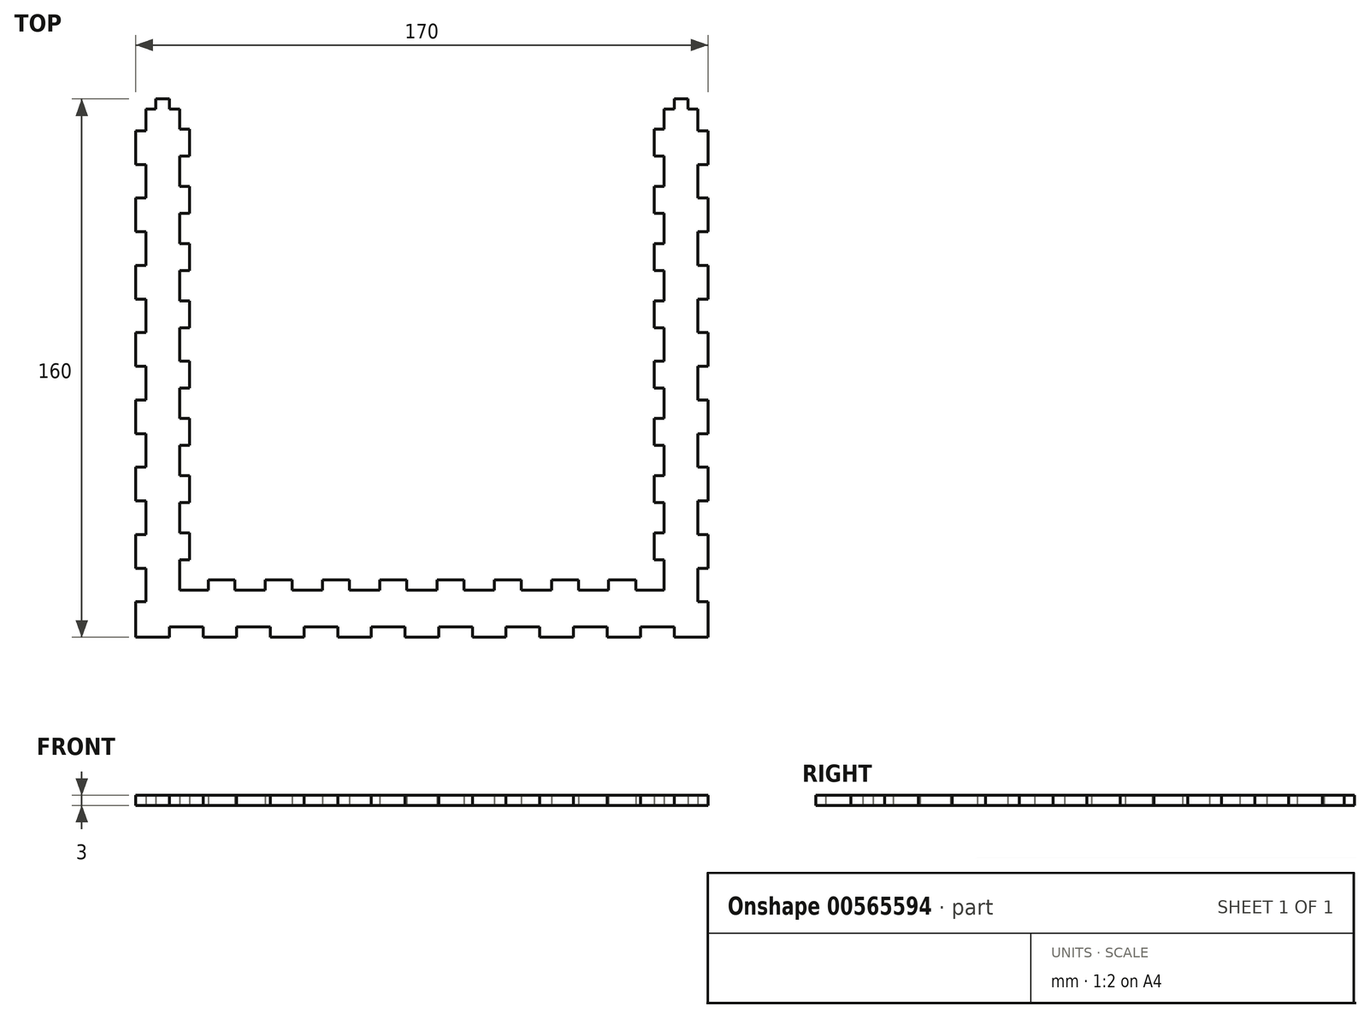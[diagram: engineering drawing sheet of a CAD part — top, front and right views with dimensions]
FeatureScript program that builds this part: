
annotation { "Feature Type Name" : "Feature", "Feature Type Description" : "" }
export const myFeature = defineFeature(function(context is Context, id is Id, definition is map)
    precondition{}
    {
        {
            var Q0;
            Q0=qCreatedBy(makeId("Top.planeOp"),FACE);
            var sketch = newSketch(context, id + "F0", { "sketchPlane" : qUnion([Q0])});
            skLineSegment(sketch, "E0.bottom", {"start": v(0, 0) * mm, "end": v(10, 0) * mm});
            skLineSegment(sketch, "E0.top", {"start": v(6, 160) * mm, "end": v(10, 160) * mm});
            skLineSegment(sketch, "E0.left", {"start": v(0, 0) * mm, "end": v(0, 10.5) * mm});
            skLineSegment(sketch, "E0.right", {"start": v(170, 0) * mm, "end": v(170, 10.5) * mm});
            skLineSegment(sketch, "E1.top", {"start": v(21.5, 17) * mm, "end": v(29.5, 17) * mm});
            skLineSegment(sketch, "E1.left", {"start": v(16, 151) * mm, "end": v(16, 143) * mm});
            skLineSegment(sketch, "E1.right", {"start": v(154, 151) * mm, "end": v(154, 143) * mm});
            skLineSegment(sketch, "E2.top", {"start": v(16, 151) * mm, "end": v(13, 151) * mm});
            skLineSegment(sketch, "E2.right", {"start": v(13, 157) * mm, "end": v(13, 151) * mm});
            skLineSegment(sketch, "E3.bottom", {"start": v(16, 143) * mm, "end": v(13, 143) * mm});
            skLineSegment(sketch, "E3.top", {"start": v(16, 134) * mm, "end": v(13, 134) * mm});
            skLineSegment(sketch, "E3.right", {"start": v(13, 143) * mm, "end": v(13, 134) * mm});
            skLineSegment(sketch, "E4.bottom", {"start": v(16, 126) * mm, "end": v(13, 126) * mm});
            skLineSegment(sketch, "E4.top", {"start": v(16, 117) * mm, "end": v(13, 117) * mm});
            skLineSegment(sketch, "E4.right", {"start": v(13, 126) * mm, "end": v(13, 117) * mm});
            skLineSegment(sketch, "E5.bottom", {"start": v(16, 109) * mm, "end": v(13, 109) * mm});
            skLineSegment(sketch, "E5.top", {"start": v(16, 100) * mm, "end": v(13, 100) * mm});
            skLineSegment(sketch, "E5.right", {"start": v(13, 109) * mm, "end": v(13, 100) * mm});
            skLineSegment(sketch, "E6.bottom", {"start": v(16, 92) * mm, "end": v(13, 92) * mm});
            skLineSegment(sketch, "E6.top", {"start": v(16, 82) * mm, "end": v(13, 82) * mm});
            skLineSegment(sketch, "E6.right", {"start": v(13, 92) * mm, "end": v(13, 82) * mm});
            skLineSegment(sketch, "E7.bottom", {"start": v(16, 74) * mm, "end": v(13, 74) * mm});
            skLineSegment(sketch, "E7.top", {"start": v(16, 65) * mm, "end": v(13, 65) * mm});
            skLineSegment(sketch, "E7.right", {"start": v(13, 74) * mm, "end": v(13, 65) * mm});
            skLineSegment(sketch, "E8.bottom", {"start": v(13, 57) * mm, "end": v(16, 57) * mm});
            skLineSegment(sketch, "E8.top", {"start": v(13, 48) * mm, "end": v(16, 48) * mm});
            skLineSegment(sketch, "E8.left", {"start": v(13, 57) * mm, "end": v(13, 48) * mm});
            skLineSegment(sketch, "E9.bottom", {"start": v(16, 40) * mm, "end": v(13, 40) * mm});
            skLineSegment(sketch, "E9.top", {"start": v(16, 31) * mm, "end": v(13, 31) * mm});
            skLineSegment(sketch, "E9.right", {"start": v(13, 40) * mm, "end": v(13, 31) * mm});
            skLineSegment(sketch, "E10.bottom", {"start": v(13, 14) * mm, "end": v(21.5, 14) * mm});
            skLineSegment(sketch, "E10.top", {"start": v(13, 23) * mm, "end": v(16, 23) * mm});
            skLineSegment(sketch, "E10.left", {"start": v(13, 14) * mm, "end": v(13, 23) * mm});
            skLineSegment(sketch, "E10.right", {"start": v(21.5, 14) * mm, "end": v(21.5, 17) * mm});
            skLineSegment(sketch, "E11.bottom", {"start": v(29.5, 14) * mm, "end": v(38.5, 14) * mm});
            skLineSegment(sketch, "E11.left", {"start": v(29.5, 14) * mm, "end": v(29.5, 17) * mm});
            skLineSegment(sketch, "E11.right", {"start": v(38.5, 14) * mm, "end": v(38.5, 17) * mm});
            skLineSegment(sketch, "E12.bottom", {"start": v(46.5, 14) * mm, "end": v(55.5, 14) * mm});
            skLineSegment(sketch, "E12.left", {"start": v(46.5, 14) * mm, "end": v(46.5, 17) * mm});
            skLineSegment(sketch, "E12.right", {"start": v(55.5, 14) * mm, "end": v(55.5, 17) * mm});
            skLineSegment(sketch, "E13.bottom", {"start": v(63.5, 14) * mm, "end": v(72.5, 14) * mm});
            skLineSegment(sketch, "E13.left", {"start": v(63.5, 14) * mm, "end": v(63.5, 17) * mm});
            skLineSegment(sketch, "E13.right", {"start": v(72.5, 14) * mm, "end": v(72.5, 17) * mm});
            skLineSegment(sketch, "E14.bottom", {"start": v(80.5, 14) * mm, "end": v(89.5, 14) * mm});
            skLineSegment(sketch, "E14.left", {"start": v(80.5, 14) * mm, "end": v(80.5, 17) * mm});
            skLineSegment(sketch, "E14.right", {"start": v(89.5, 14) * mm, "end": v(89.5, 17) * mm});
            skLineSegment(sketch, "E15.bottom", {"start": v(97.5, 14) * mm, "end": v(106.5, 14) * mm});
            skLineSegment(sketch, "E15.left", {"start": v(97.5, 14) * mm, "end": v(97.5, 17) * mm});
            skLineSegment(sketch, "E15.right", {"start": v(106.5, 14) * mm, "end": v(106.5, 17) * mm});
            skLineSegment(sketch, "E16.bottom", {"start": v(114.5, 14) * mm, "end": v(123.5, 14) * mm});
            skLineSegment(sketch, "E16.left", {"start": v(114.5, 14) * mm, "end": v(114.5, 17) * mm});
            skLineSegment(sketch, "E16.right", {"start": v(123.5, 14) * mm, "end": v(123.5, 17) * mm});
            skLineSegment(sketch, "E17.bottom", {"start": v(131.5, 14) * mm, "end": v(140.5, 14) * mm});
            skLineSegment(sketch, "E17.left", {"start": v(131.5, 14) * mm, "end": v(131.5, 17) * mm});
            skLineSegment(sketch, "E17.right", {"start": v(140.5, 14) * mm, "end": v(140.5, 17) * mm});
            skLineSegment(sketch, "E18.bottom", {"start": v(148.5, 14) * mm, "end": v(157, 14) * mm});
            skLineSegment(sketch, "E18.top", {"start": v(154, 23) * mm, "end": v(157, 23) * mm});
            skLineSegment(sketch, "E18.left", {"start": v(148.5, 14) * mm, "end": v(148.5, 17) * mm});
            skLineSegment(sketch, "E18.right", {"start": v(157, 14) * mm, "end": v(157, 23) * mm});
            skLineSegment(sketch, "E19.bottom", {"start": v(157, 31) * mm, "end": v(154, 31) * mm});
            skLineSegment(sketch, "E19.top", {"start": v(157, 40) * mm, "end": v(154, 40) * mm});
            skLineSegment(sketch, "E19.left", {"start": v(157, 31) * mm, "end": v(157, 40) * mm});
            skLineSegment(sketch, "E20.bottom", {"start": v(157, 48) * mm, "end": v(154, 48) * mm});
            skLineSegment(sketch, "E20.top", {"start": v(157, 57) * mm, "end": v(154, 57) * mm});
            skLineSegment(sketch, "E20.left", {"start": v(157, 48) * mm, "end": v(157, 57) * mm});
            skLineSegment(sketch, "E21.bottom", {"start": v(157, 65) * mm, "end": v(154, 65) * mm});
            skLineSegment(sketch, "E21.top", {"start": v(157, 74) * mm, "end": v(154, 74) * mm});
            skLineSegment(sketch, "E21.left", {"start": v(157, 65) * mm, "end": v(157, 74) * mm});
            skLineSegment(sketch, "E22.bottom", {"start": v(157, 82) * mm, "end": v(154, 82) * mm});
            skLineSegment(sketch, "E22.top", {"start": v(157, 92) * mm, "end": v(154, 92) * mm});
            skLineSegment(sketch, "E22.left", {"start": v(157, 82) * mm, "end": v(157, 92) * mm});
            skLineSegment(sketch, "E23.bottom", {"start": v(157, 100) * mm, "end": v(154, 100) * mm});
            skLineSegment(sketch, "E23.top", {"start": v(157, 109) * mm, "end": v(154, 109) * mm});
            skLineSegment(sketch, "E23.left", {"start": v(157, 100) * mm, "end": v(157, 109) * mm});
            skLineSegment(sketch, "E24.bottom", {"start": v(157, 117) * mm, "end": v(154, 117) * mm});
            skLineSegment(sketch, "E24.top", {"start": v(157, 126) * mm, "end": v(154, 126) * mm});
            skLineSegment(sketch, "E24.left", {"start": v(157, 117) * mm, "end": v(157, 126) * mm});
            skLineSegment(sketch, "E25.bottom", {"start": v(157, 134) * mm, "end": v(154, 134) * mm});
            skLineSegment(sketch, "E25.top", {"start": v(157, 143) * mm, "end": v(154, 143) * mm});
            skLineSegment(sketch, "E25.left", {"start": v(157, 134) * mm, "end": v(157, 143) * mm});
            skLineSegment(sketch, "E26.bottom", {"start": v(157, 151) * mm, "end": v(154, 151) * mm});
            skLineSegment(sketch, "E26.left", {"start": v(157, 151) * mm, "end": v(157, 157) * mm});
            skLineSegment(sketch, "E27.top", {"start": v(13, 157) * mm, "end": v(10, 157) * mm});
            skLineSegment(sketch, "E27.right", {"start": v(10, 160) * mm, "end": v(10, 157) * mm});
            skLineSegment(sketch, "E28.top", {"start": v(3, 157) * mm, "end": v(6, 157) * mm});
            skLineSegment(sketch, "E28.right", {"start": v(6, 160) * mm, "end": v(6, 157) * mm});
            skLineSegment(sketch, "E29.top", {"start": v(0, 150.5) * mm, "end": v(3, 150.5) * mm});
            skLineSegment(sketch, "E29.right", {"start": v(3, 157) * mm, "end": v(3, 150.5) * mm});
            skLineSegment(sketch, "E30.bottom", {"start": v(3, 140.5) * mm, "end": v(0, 140.5) * mm});
            skLineSegment(sketch, "E30.top", {"start": v(3, 130.5) * mm, "end": v(0, 130.5) * mm});
            skLineSegment(sketch, "E30.left", {"start": v(3, 140.5) * mm, "end": v(3, 130.5) * mm});
            skLineSegment(sketch, "E31.bottom", {"start": v(3, 120.5) * mm, "end": v(0, 120.5) * mm});
            skLineSegment(sketch, "E31.top", {"start": v(3, 110.5) * mm, "end": v(0, 110.5) * mm});
            skLineSegment(sketch, "E31.left", {"start": v(3, 120.5) * mm, "end": v(3, 110.5) * mm});
            skLineSegment(sketch, "E32.bottom", {"start": v(3, 100.5) * mm, "end": v(0, 100.5) * mm});
            skLineSegment(sketch, "E32.top", {"start": v(3, 90.5) * mm, "end": v(0, 90.5) * mm});
            skLineSegment(sketch, "E32.left", {"start": v(3, 100.5) * mm, "end": v(3, 90.5) * mm});
            skLineSegment(sketch, "E33.bottom", {"start": v(3, 80.5) * mm, "end": v(0, 80.5) * mm});
            skLineSegment(sketch, "E33.top", {"start": v(3, 70.5) * mm, "end": v(0, 70.5) * mm});
            skLineSegment(sketch, "E33.left", {"start": v(3, 80.5) * mm, "end": v(3, 70.5) * mm});
            skLineSegment(sketch, "E34.bottom", {"start": v(3, 60.5) * mm, "end": v(0, 60.5) * mm});
            skLineSegment(sketch, "E34.top", {"start": v(3, 50.5) * mm, "end": v(0, 50.5) * mm});
            skLineSegment(sketch, "E34.left", {"start": v(3, 60.5) * mm, "end": v(3, 50.5) * mm});
            skLineSegment(sketch, "E35.bottom", {"start": v(3, 40.5) * mm, "end": v(0, 40.5) * mm});
            skLineSegment(sketch, "E35.top", {"start": v(3, 30.5) * mm, "end": v(0, 30.5) * mm});
            skLineSegment(sketch, "E35.left", {"start": v(3, 40.5) * mm, "end": v(3, 30.5) * mm});
            skLineSegment(sketch, "E36.bottom", {"start": v(3, 20.5) * mm, "end": v(0, 20.5) * mm});
            skLineSegment(sketch, "E36.top", {"start": v(3, 10.5) * mm, "end": v(0, 10.5) * mm});
            skLineSegment(sketch, "E36.left", {"start": v(3, 20.5) * mm, "end": v(3, 10.5) * mm});
            skLineSegment(sketch, "E37.top", {"start": v(10, 3) * mm, "end": v(20, 3) * mm});
            skLineSegment(sketch, "E37.left", {"start": v(10, 0) * mm, "end": v(10, 3) * mm});
            skLineSegment(sketch, "E37.right", {"start": v(20, 0) * mm, "end": v(20, 3) * mm});
            skLineSegment(sketch, "E38.bottom", {"start": v(30, 3) * mm, "end": v(40, 3) * mm});
            skLineSegment(sketch, "E38.left", {"start": v(30, 3) * mm, "end": v(30, 0) * mm});
            skLineSegment(sketch, "E38.right", {"start": v(40, 3) * mm, "end": v(40, 0) * mm});
            skLineSegment(sketch, "E39.bottom", {"start": v(50, 3) * mm, "end": v(60, 3) * mm});
            skLineSegment(sketch, "E39.left", {"start": v(50, 3) * mm, "end": v(50, 0) * mm});
            skLineSegment(sketch, "E39.right", {"start": v(60, 3) * mm, "end": v(60, 0) * mm});
            skLineSegment(sketch, "E40.bottom", {"start": v(70, 3) * mm, "end": v(80, 3) * mm});
            skLineSegment(sketch, "E40.left", {"start": v(70, 3) * mm, "end": v(70, 0) * mm});
            skLineSegment(sketch, "E40.right", {"start": v(80, 3) * mm, "end": v(80, 0) * mm});
            skLineSegment(sketch, "E41.bottom", {"start": v(90, 3) * mm, "end": v(100, 3) * mm});
            skLineSegment(sketch, "E41.left", {"start": v(90, 3) * mm, "end": v(90, 0) * mm});
            skLineSegment(sketch, "E41.right", {"start": v(100, 3) * mm, "end": v(100, 0) * mm});
            skLineSegment(sketch, "E42.bottom", {"start": v(110, 3) * mm, "end": v(120, 3) * mm});
            skLineSegment(sketch, "E42.left", {"start": v(110, 3) * mm, "end": v(110, 0) * mm});
            skLineSegment(sketch, "E42.right", {"start": v(120, 3) * mm, "end": v(120, 0) * mm});
            skLineSegment(sketch, "E43.bottom", {"start": v(130, 3) * mm, "end": v(140, 3) * mm});
            skLineSegment(sketch, "E43.left", {"start": v(130, 3) * mm, "end": v(130, 0) * mm});
            skLineSegment(sketch, "E43.right", {"start": v(140, 3) * mm, "end": v(140, 0) * mm});
            skLineSegment(sketch, "E44.bottom", {"start": v(150, 3) * mm, "end": v(160, 3) * mm});
            skLineSegment(sketch, "E44.left", {"start": v(150, 3) * mm, "end": v(150, 0) * mm});
            skLineSegment(sketch, "E44.right", {"start": v(160, 3) * mm, "end": v(160, 0) * mm});
            skLineSegment(sketch, "E45.bottom", {"start": v(170, 10.5) * mm, "end": v(167, 10.5) * mm});
            skLineSegment(sketch, "E45.top", {"start": v(170, 20.5) * mm, "end": v(167, 20.5) * mm});
            skLineSegment(sketch, "E45.right", {"start": v(167, 10.5) * mm, "end": v(167, 20.5) * mm});
            skLineSegment(sketch, "E46.bottom", {"start": v(170, 30.5) * mm, "end": v(167, 30.5) * mm});
            skLineSegment(sketch, "E46.top", {"start": v(170, 40.5) * mm, "end": v(167, 40.5) * mm});
            skLineSegment(sketch, "E46.right", {"start": v(167, 30.5) * mm, "end": v(167, 40.5) * mm});
            skLineSegment(sketch, "E47.bottom", {"start": v(167, 50.5) * mm, "end": v(170, 50.5) * mm});
            skLineSegment(sketch, "E47.top", {"start": v(167, 60.5) * mm, "end": v(170, 60.5) * mm});
            skLineSegment(sketch, "E47.left", {"start": v(167, 50.5) * mm, "end": v(167, 60.5) * mm});
            skLineSegment(sketch, "E48.bottom", {"start": v(167, 70.5) * mm, "end": v(170, 70.5) * mm});
            skLineSegment(sketch, "E48.top", {"start": v(167, 80.5) * mm, "end": v(170, 80.5) * mm});
            skLineSegment(sketch, "E48.left", {"start": v(167, 70.5) * mm, "end": v(167, 80.5) * mm});
            skLineSegment(sketch, "E49.bottom", {"start": v(167, 90.5) * mm, "end": v(170, 90.5) * mm});
            skLineSegment(sketch, "E49.top", {"start": v(167, 100.5) * mm, "end": v(170, 100.5) * mm});
            skLineSegment(sketch, "E49.left", {"start": v(167, 90.5) * mm, "end": v(167, 100.5) * mm});
            skLineSegment(sketch, "E50.bottom", {"start": v(167, 110.5) * mm, "end": v(170, 110.5) * mm});
            skLineSegment(sketch, "E50.top", {"start": v(167, 120.5) * mm, "end": v(170, 120.5) * mm});
            skLineSegment(sketch, "E50.left", {"start": v(167, 110.5) * mm, "end": v(167, 120.5) * mm});
            skLineSegment(sketch, "E51.bottom", {"start": v(167, 130.5) * mm, "end": v(170, 130.5) * mm});
            skLineSegment(sketch, "E51.top", {"start": v(167, 140.5) * mm, "end": v(170, 140.5) * mm});
            skLineSegment(sketch, "E51.left", {"start": v(167, 130.5) * mm, "end": v(167, 140.5) * mm});
            skLineSegment(sketch, "E52.top", {"start": v(170, 150.5) * mm, "end": v(167, 150.5) * mm});
            skLineSegment(sketch, "E52.right", {"start": v(167, 157) * mm, "end": v(167, 150.5) * mm});
            skLineSegment(sketch, "E53.top", {"start": v(167, 157) * mm, "end": v(164, 157) * mm});
            skLineSegment(sketch, "E53.right", {"start": v(164, 160) * mm, "end": v(164, 157) * mm});
            skLineSegment(sketch, "E54.top", {"start": v(157, 157) * mm, "end": v(160, 157) * mm});
            skLineSegment(sketch, "E54.right", {"start": v(160, 160) * mm, "end": v(160, 157) * mm});
            skLineSegment(sketch, "E55.trimOffspring", {"start": v(160, 160) * mm, "end": v(164, 160) * mm});
            skLineSegment(sketch, "E56.trimOffspring", {"start": v(38.5, 17) * mm, "end": v(46.5, 17) * mm});
            skLineSegment(sketch, "E57.trimOffspring", {"start": v(16, 31) * mm, "end": v(16, 23) * mm});
            skLineSegment(sketch, "E58.trimOffspring", {"start": v(123.5, 17) * mm, "end": v(131.5, 17) * mm});
            skLineSegment(sketch, "E59.trimOffspring", {"start": v(140.5, 17) * mm, "end": v(148.5, 17) * mm});
            skLineSegment(sketch, "E60.trimOffspring", {"start": v(106.5, 17) * mm, "end": v(114.5, 17) * mm});
            skLineSegment(sketch, "E61.trimOffspring", {"start": v(89.5, 17) * mm, "end": v(97.5, 17) * mm});
            skLineSegment(sketch, "E62.trimOffspring", {"start": v(72.5, 17) * mm, "end": v(80.5, 17) * mm});
            skLineSegment(sketch, "E63.trimOffspring", {"start": v(55.5, 17) * mm, "end": v(63.5, 17) * mm});
            skLineSegment(sketch, "E64.trimOffspring", {"start": v(16, 48) * mm, "end": v(16, 40) * mm});
            skLineSegment(sketch, "E65.trimOffspring", {"start": v(0, 40.5) * mm, "end": v(0, 50.5) * mm});
            skLineSegment(sketch, "E66.trimOffspring", {"start": v(0, 60.5) * mm, "end": v(0, 70.5) * mm});
            skLineSegment(sketch, "E67.trimOffspring", {"start": v(0, 140.5) * mm, "end": v(0, 150.5) * mm});
            skLineSegment(sketch, "E68.trimOffspring", {"start": v(16, 134) * mm, "end": v(16, 126) * mm});
            skLineSegment(sketch, "E69.trimOffspring", {"start": v(16, 117) * mm, "end": v(16, 109) * mm});
            skLineSegment(sketch, "E70.trimOffspring", {"start": v(0, 120.5) * mm, "end": v(0, 130.5) * mm});
            skLineSegment(sketch, "E71.trimOffspring", {"start": v(16, 100) * mm, "end": v(16, 92) * mm});
            skLineSegment(sketch, "E72.trimOffspring", {"start": v(0, 100.5) * mm, "end": v(0, 110.5) * mm});
            skLineSegment(sketch, "E73.trimOffspring", {"start": v(16, 82) * mm, "end": v(16, 74) * mm});
            skLineSegment(sketch, "E74.trimOffspring", {"start": v(0, 80.5) * mm, "end": v(0, 90.5) * mm});
            skLineSegment(sketch, "E75.trimOffspring", {"start": v(16, 65) * mm, "end": v(16, 57) * mm});
            skLineSegment(sketch, "E76.trimOffspring", {"start": v(0, 20.5) * mm, "end": v(0, 30.5) * mm});
            skLineSegment(sketch, "E77.trimOffspring", {"start": v(20, 0) * mm, "end": v(30, 0) * mm});
            skLineSegment(sketch, "E78.trimOffspring", {"start": v(40, 0) * mm, "end": v(50, 0) * mm});
            skLineSegment(sketch, "E79.trimOffspring", {"start": v(60, 0) * mm, "end": v(70, 0) * mm});
            skLineSegment(sketch, "E80.trimOffspring", {"start": v(80, 0) * mm, "end": v(90, 0) * mm});
            skLineSegment(sketch, "E81.trimOffspring", {"start": v(100, 0) * mm, "end": v(110, 0) * mm});
            skLineSegment(sketch, "E82.trimOffspring", {"start": v(120, 0) * mm, "end": v(130, 0) * mm});
            skLineSegment(sketch, "E83.trimOffspring", {"start": v(140, 0) * mm, "end": v(150, 0) * mm});
            skLineSegment(sketch, "E84.trimOffspring", {"start": v(160, 0) * mm, "end": v(170, 0) * mm});
            skLineSegment(sketch, "E85.trimOffspring", {"start": v(170, 20.5) * mm, "end": v(170, 30.5) * mm});
            skLineSegment(sketch, "E86.trimOffspring", {"start": v(170, 40.5) * mm, "end": v(170, 50.5) * mm});
            skLineSegment(sketch, "E87.trimOffspring", {"start": v(154, 31) * mm, "end": v(154, 23) * mm});
            skLineSegment(sketch, "E88.trimOffspring", {"start": v(154, 48) * mm, "end": v(154, 40) * mm});
            skLineSegment(sketch, "E89.trimOffspring", {"start": v(170, 60.5) * mm, "end": v(170, 70.5) * mm});
            skLineSegment(sketch, "E90.trimOffspring", {"start": v(170, 80.5) * mm, "end": v(170, 90.5) * mm});
            skLineSegment(sketch, "E91.trimOffspring", {"start": v(154, 65) * mm, "end": v(154, 57) * mm});
            skLineSegment(sketch, "E92.trimOffspring", {"start": v(154, 82) * mm, "end": v(154, 74) * mm});
            skLineSegment(sketch, "E93.trimOffspring", {"start": v(170, 100.5) * mm, "end": v(170, 110.5) * mm});
            skLineSegment(sketch, "E94.trimOffspring", {"start": v(154, 100) * mm, "end": v(154, 92) * mm});
            skLineSegment(sketch, "E95.trimOffspring", {"start": v(170, 120.5) * mm, "end": v(170, 130.5) * mm});
            skLineSegment(sketch, "E96.trimOffspring", {"start": v(154, 117) * mm, "end": v(154, 109) * mm});
            skLineSegment(sketch, "E97.trimOffspring", {"start": v(154, 134) * mm, "end": v(154, 126) * mm});
            skLineSegment(sketch, "E98.trimOffspring", {"start": v(170, 140.5) * mm, "end": v(170, 150.5) * mm});
            skPoint(sketch, "E26.top.end.orphan", {"position": v(154, 160) * mm});
            skSolve(sketch);
        }
        {
            var Q0;
            Q0=makeQuery(id+"F0.imprint","IMPRINT",FACE,{"disambiguationData":[TD([[makeQuery(id+"F0.imprint","IMPRINT",EDGE,{"derivedFrom":sQuery(id+"F0.wireOp",EDGE,"E0.bottom")}),1.0]])]});
            extrude(context, id + "F1", {"entities" : qUnion([Q0]), "depth" : 3 * mm, "offsetDistance" : 25 * mm});
        }
    });
